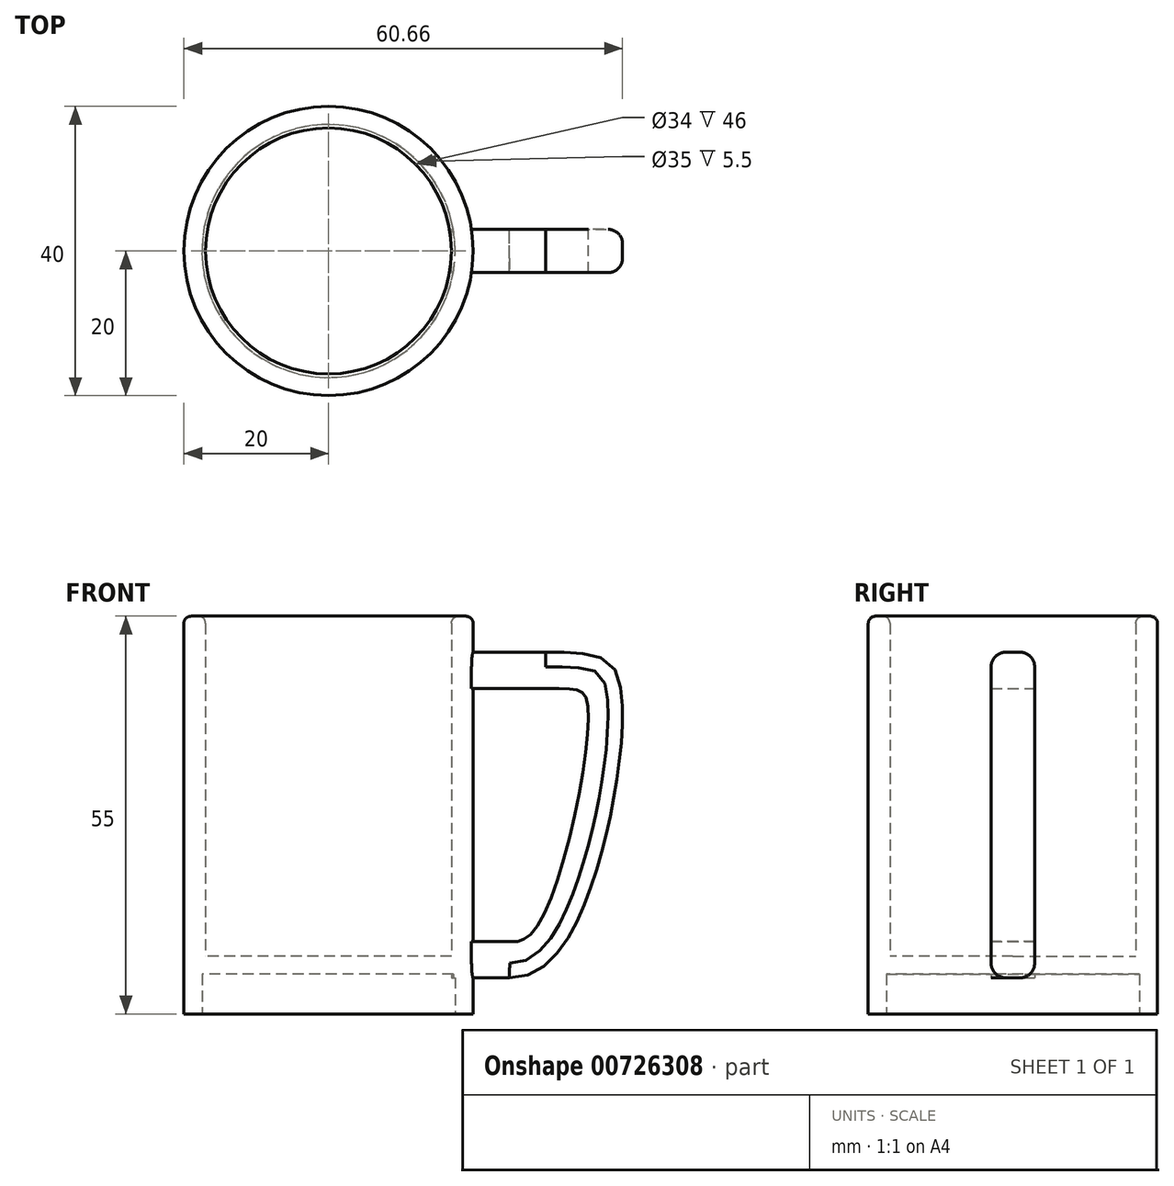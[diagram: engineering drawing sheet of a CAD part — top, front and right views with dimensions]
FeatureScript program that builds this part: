
annotation { "Feature Type Name" : "Feature", "Feature Type Description" : "" }
export const myFeature = defineFeature(function(context is Context, id is Id, definition is map)
    precondition{}
    {
        {
            var Q0;
            Q0=qCreatedBy(makeId("Front.planeOp"),FACE);
            var sketch = newSketch(context, id + "F0", { "sketchPlane" : qUnion([Q0])});
            skLineSegment(sketch, "E0", {"start": v(0, 0) * mm, "end": v(0, 50) * mm});
            skLineSegment(sketch, "E1", {"start": v(0, 50) * mm, "end": v(20, 50) * mm});
            skLineSegment(sketch, "E2", {"start": v(20, 50) * mm, "end": v(20, 0) * mm});
            skLineSegment(sketch, "E3", {"start": v(20, 0) * mm, "end": v(0, 0) * mm});
            skSolve(sketch);
        }
        {
            var Q0;
            Q0 = qSketchRegion(id + "F0", true);
            var Q1;
            Q1=sQuery(id+"F0.wireOp",EDGE,"E0");
            revolve(context, id + "F1", {"surfaceOperationType" : NewSurfaceOperationType.NEW, "entities" : qUnion([Q0]), "axis" : qUnion([Q1]), "revolveType" : RevolveType.FULL});
        }
        {
            var Q0;
            Q0=makeQuery(id+"F1.opRevolve","SWEPT_FACE",FACE,{"disambiguationData":[OSD([sQuery(id+"F0.wireOp",EDGE,"E1")])]});
            var Q1;
            Q1=makeQuery(id+"F1.opRevolve","SWEPT_BODY",BODY,{"disambiguationData":[OSD([sQuery(id+"F0.wireOp",EDGE,"E0"),sQuery(id+"F0.wireOp",EDGE,"E1"),sQuery(id+"F0.wireOp",EDGE,"E2"),sQuery(id+"F0.wireOp",EDGE,"E3")])]});
            shell(context, id + "F2", {"entities" : qUnion([Q0]), "parts" : qUnion([Q1]), "thickness" : 3 * mm});
        }
        {
            var Q0;
            Q0=qCreatedBy(makeId("Front.planeOp"),FACE);
            var sketch = newSketch(context, id + "F3", { "sketchPlane" : qUnion([Q0])});
            skLineSegment(sketch, "E4", {"start": v(0, 0) * mm, "end": v(0, -5) * mm});
            skSolve(sketch);
        }
        {
            var Q0;
            Q0=makeQuery(id+"F1.opRevolve","SWEPT_FACE",FACE,{"disambiguationData":[OSD([sQuery(id+"F0.wireOp",EDGE,"E3")])]});
            var Q1;
            Q1=sQuery(id+"F3.wireOp",EDGE,"E4");
            sweep(context, id + "F4", {"operationType" : NewBodyOperationType.ADD, "profiles" : qUnion([Q0]), "path" : qUnion([Q1])});
        }
        {
            var Q0;
            Q0=makeQuery(id+"F4.opSweep","CAP_FACE",FACE,{"disambiguationData":[OSD([sQuery(id+"F0.wireOp",EDGE,"E3"),sQuery(id+"F3.wireOp",VERTEX,"E4.end")])],"isStart":false});
            shell(context, id + "F5", {"entities" : qUnion([Q0]), "thickness" : 2.5 * mm});
        }
        {
            var Q0;
            Q0=qCreatedBy(makeId("Front.planeOp"),FACE);
            var sketch = newSketch(context, id + "F6", { "sketchPlane" : qUnion([Q0])});
            skLineSegment(sketch, "E5", {"start": v(20, 45) * mm, "end": v(30, 45) * mm});
            skLineSegment(sketch, "E6", {"start": v(30, 45) * mm, "end": v(30, 40) * mm});
            skLineSegment(sketch, "E7", {"start": v(30, 40) * mm, "end": v(20, 40) * mm});
            skLineSegment(sketch, "E8", {"start": v(20, 40) * mm, "end": v(20, 45) * mm});
            skLineSegment(sketch, "E9", {"start": v(20, 0) * mm, "end": v(25, 0) * mm});
            skLineSegment(sketch, "E10", {"start": v(25, 0) * mm, "end": v(25, 5) * mm});
            skLineSegment(sketch, "E11", {"start": v(25, 5) * mm, "end": v(20, 5) * mm});
            skLineSegment(sketch, "E12", {"start": v(20, 5) * mm, "end": v(20, 0) * mm});
            skLineSegment(sketch, "E13", {"start": v(20, 45) * mm, "end": v(17, 45) * mm});
            skLineSegment(sketch, "E14", {"start": v(17, 45) * mm, "end": v(17, 40) * mm});
            skPoint(sketch, "E14.endSnap0", {"position": v(25, 40) * mm});
            skLineSegment(sketch, "E15", {"start": v(17, 40) * mm, "end": v(20, 40) * mm});
            skLineSegment(sketch, "E16", {"start": v(20, 5) * mm, "end": v(17, 5) * mm});
            skLineSegment(sketch, "E17", {"start": v(17, 5) * mm, "end": v(17, 0) * mm});
            skLineSegment(sketch, "E18", {"start": v(17, 0) * mm, "end": v(20, 0) * mm});
            skFitSpline(sketch, "E19", {"points": [v(30, 45) * mm, v(40.48, 39.7) * mm, v(33, 5.3) * mm, v(25, 0) * mm], "startDerivative": vector(84.35, 1.6) * mm, "endDerivative": vector(-29.46, 1.86) * mm});
            skFitSpline(sketch, "E20", {"points": [v(30, 40) * mm, v(35.79, 37.97) * mm, v(28.07, 6.1) * mm, v(25, 5) * mm], "startDerivative": vector(48.2, -1.77) * mm, "endDerivative": vector(-7.66, -0.86) * mm});
            skSolve(sketch);
        }
        {
            var Q0;
            Q0 = qSketchRegion(id + "F6", true);
            extrude(context, id + "F7", {"entities" : qUnion([Q0]), "operationType" : NewBodyOperationType.ADD, "endBound" : BoundingType.SYMMETRIC, "depth" : 6 * mm, "offsetDistance" : 25 * mm});
        }
        {
            var Q0;
            Q0=makeQuery(id+"F7.opExtrude","CAP_EDGE",EDGE,{"disambiguationData":[OSD([sQuery(id+"F6.wireOp",EDGE,"E5"),sQuery(id+"F6.wireOp",EDGE,"E13")])],"isStart":false});
            var Q1;
            Q1=makeQuery(id+"F7.opExtrude","CAP_EDGE",EDGE,{"disambiguationData":[OSD([sQuery(id+"F6.wireOp",EDGE,"E5"),sQuery(id+"F6.wireOp",EDGE,"E13")])],"isStart":true});
            fillet(context, id + "F8", {"entities" : qUnion([Q0, Q1]), "radius" : 2 * mm, "tangentPropagation" : true, "allowEdgeOverflow" : false});
        }
        {
            var Q0;
            Q0=makeQuery(id+"F1.opRevolve","SWEPT_EDGE",EDGE,{"disambiguationData":[OSD([sQuery(id+"F0.wireOp",EDGE,"E1"),sQuery(id+"F0.wireOp",EDGE,"E2")])]});
            var Q1;
            Q1=makeQuery(id+"F2.opShell","OFFSET_EDGE",EDGE,{"disambiguationData":[OSD([sQuery(id+"F0.wireOp",EDGE,"E1"),sQuery(id+"F0.wireOp",EDGE,"E2")])]});
            fillet(context, id + "F9", {"entities" : qUnion([Q0, Q1]), "radius" : 1 * mm, "tangentPropagation" : true, "allowEdgeOverflow" : false});
        }
    });
